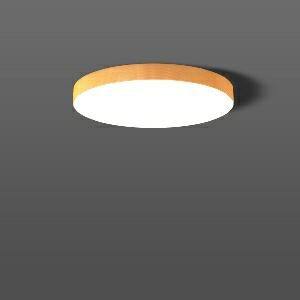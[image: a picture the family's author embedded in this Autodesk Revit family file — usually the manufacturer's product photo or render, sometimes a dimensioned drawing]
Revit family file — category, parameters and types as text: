
# Revit family: flatliner_slim_312283_002_91c9
name_source: partatom
category: Lighting Fixtures
units: mm (PartAtom-declared; Revit-internal decimal feet)

## family parameters
Cut with Voids When Loaded = No
Host = Face
Light Source = No
Part Type = Normal
Room Calculation Point = No
Round Connector Dimension = Use Diameter
Shared = No

## types (1)
- 982557.002 (1 x LED Modul 830, 1900 lm, 3000)
    Apparent Load = 24 VA
    CIE Flux Codes = 45 76 94 95 100
    Color Rendering = 80
    Color Temperature = 3000
    Default Elevation = 1800 mm
    Description = Series: FLATLINER SLIM
Decorative ceiling luminaire for interior decoration. Base luminaire prepared for the installation of fabric lampshade. Base: metal, white, powder-coated. Modular design: with the basic luminaire, a cylindrical fabric lampshade with a polycarbonate satin-finish diffuser must always be ordered separately. Fabric lampshade and diffuser can be assembled without the use of tools. 
Colour: white
Diameter: 418 mm
Height: 34 mm
Lamp: LED exchangeable
Socket: without socket
Colour temperature: 3000K
Colour rendering index (CRI): 83
System power: 24 W
Rated luminous flux: 1900 lm
Beam angle Down: 117°
Luminous efficiency: 79 lm/W
Control gear: AC Strom, dim.Ph.an-/abschnitt
Protection class: I
Type of protection: IP 20
    Height = 34 mm  [stored 0.111549 ft]
    Lamp = 1 x LED Modul 830
    Lamp Light Flux = 1900 lm
    Lamp count = 1
    Length = 418 mm
    Lifetime = 50000 h
    Luminous efficacy = 79 lm/W
    Manufacturer = RZB
    ModVariant = No
    Model = 312283.002
    Mounting Place = Ceiling
    Mounting Type = Surface mounted
    Number of Poles = 1
    OnlyDefault = Yes
    Power Factor = 1
    Product Name = FLATLINER SLIM
    Product group = Surface mounted ceiling Fabric lampshade luminaires
    ProductGroupID = 313
    Protection Class = Protection class I
    Protection Degree = IP 20
    RLX_Detail_Level = 1
    RLX_Emergency_Light_Flux = 0 lm
    RLX_Emergency_Type = 0
    RLX_Emergency_Type_DB = No
    RlxData = <blob elided: 25401 chars, md5=31d4f461>
    Socket = socket
    Standby Power = 0 W
    System Light Flux = 1900 lm
    System Power = 24 W
    Type Image = 312287.002_982442.0063_982444.002.jpg
    URL = http://relux.com
    VarID = 982557_002_b87f
    Voltage = 230 V
    Voltage Range = 220-240 V
    Weight = 0.00 kg
    Width = 0 mm  [stored 0 ft]

note: [stored X ft] marks values corroborated as IEEE doubles in the binary element streams (Revit-internal decimal feet)

## geometry (parser evidence)
native form markers: Blend x4, Sweep x12
no freeform markers — native parametric forms only
